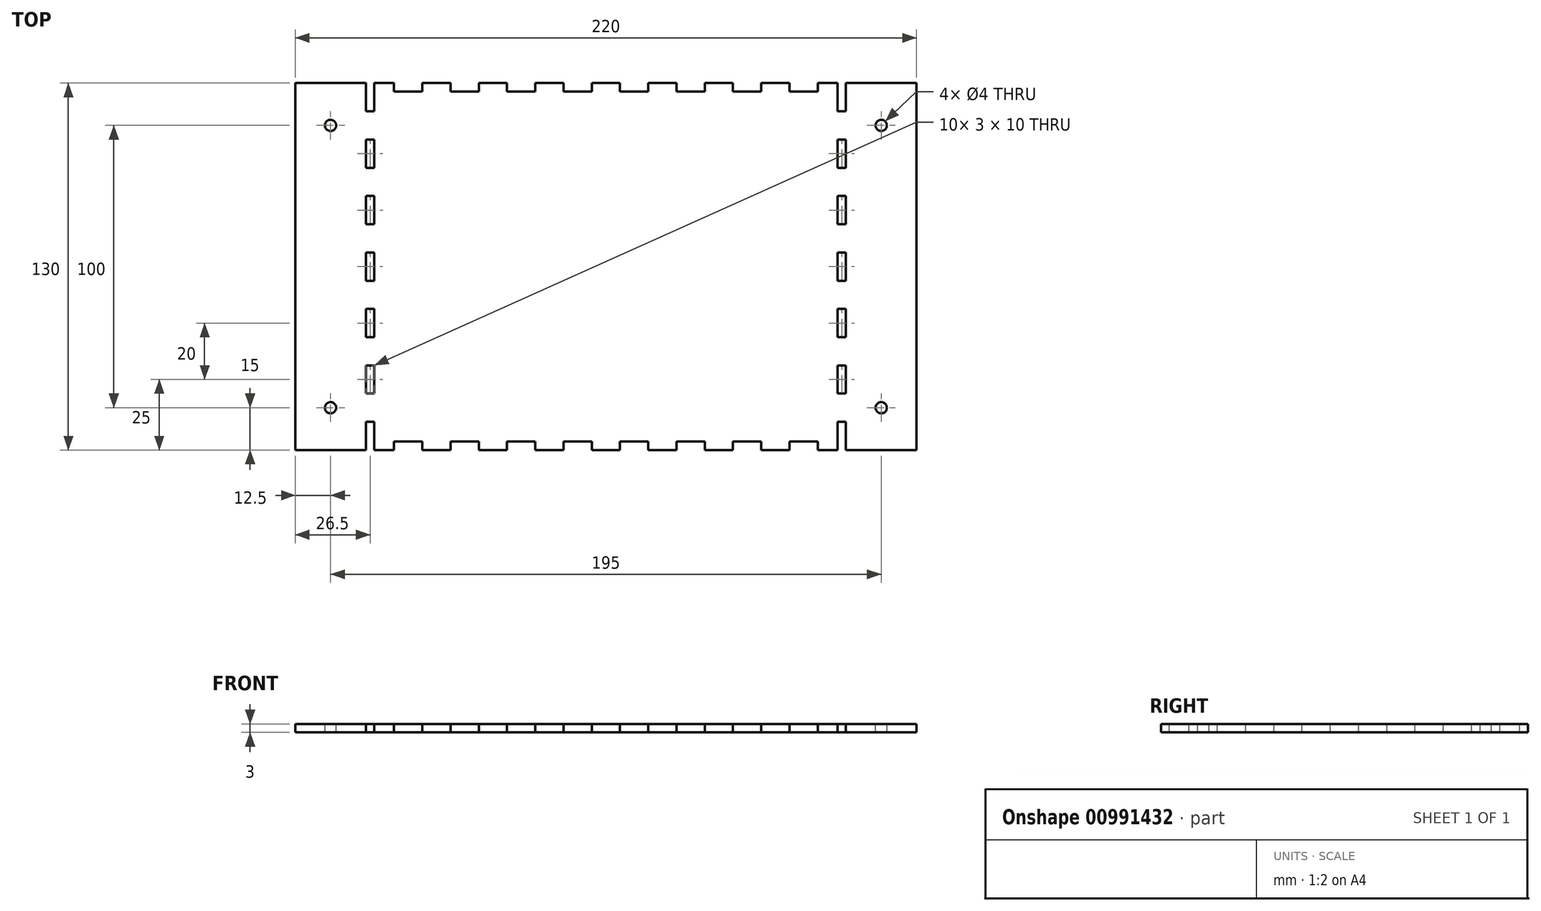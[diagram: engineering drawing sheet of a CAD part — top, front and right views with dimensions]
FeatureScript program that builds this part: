
annotation { "Feature Type Name" : "Feature", "Feature Type Description" : "" }
export const myFeature = defineFeature(function(context is Context, id is Id, definition is map)
    precondition{}
    {
        {
            var Q0;
            Q0=qCreatedBy(makeId("Top.planeOp"),FACE);
            var sketch = newSketch(context, id + "F0", { "sketchPlane" : qUnion([Q0])});
            skLineSegment(sketch, "E0.bottom", {"start": v(110, -65) * mm, "end": v(-110, -65) * mm});
            skLineSegment(sketch, "E0.top", {"start": v(110, 65) * mm, "end": v(-110, 65) * mm});
            skLineSegment(sketch, "E0.left", {"start": v(110, -65) * mm, "end": v(110, 65) * mm});
            skLineSegment(sketch, "E0.right", {"start": v(-110, -65) * mm, "end": v(-110, 65) * mm});
            skPoint(sketch, "E0.middle", {"position": v(0, 0) * mm});
            skSolve(sketch);
        }
        {
            var Q0;
            Q0 = qSketchRegion(id + "F0", true);
            extrude(context, id + "F1", {"entities" : qUnion([Q0]), "depth" : 3 * mm, "offsetDistance" : 25 * mm});
        }
        {
            var Q0;
            Q0=makeQuery(id+"F1.opExtrude","CAP_FACE",FACE,{"disambiguationData":[OSD([sQuery(id+"F0.wireOp",EDGE,"E0.bottom"),sQuery(id+"F0.wireOp",EDGE,"E0.top"),sQuery(id+"F0.wireOp",EDGE,"E0.left"),sQuery(id+"F0.wireOp",EDGE,"E0.right")])],"isStart":false});
            var sketch = newSketch(context, id + "F2", { "sketchPlane" : qUnion([Q0])});
            skLineSegment(sketch, "E1.bottom", {"start": v(-75, -65) * mm, "end": v(-65, -65) * mm});
            skLineSegment(sketch, "E1.top", {"start": v(-75, -62) * mm, "end": v(-65, -62) * mm});
            skLineSegment(sketch, "E1.right", {"start": v(-65, -65) * mm, "end": v(-65, -62) * mm});
            skLineSegment(sketch, "E2.1.0.0", {"start": v(-55, -65) * mm, "end": v(-45, -65) * mm});
            skLineSegment(sketch, "E2.1.0.1", {"start": v(-55, -62) * mm, "end": v(-45, -62) * mm});
            skLineSegment(sketch, "E2.1.0.2", {"start": v(-55, -65) * mm, "end": v(-55, -62) * mm});
            skLineSegment(sketch, "E2.1.0.3", {"start": v(-45, -65) * mm, "end": v(-45, -62) * mm});
            skLineSegment(sketch, "E2.2.0.0", {"start": v(-35, -65) * mm, "end": v(-25, -65) * mm});
            skLineSegment(sketch, "E2.2.0.1", {"start": v(-35, -62) * mm, "end": v(-25, -62) * mm});
            skLineSegment(sketch, "E2.2.0.2", {"start": v(-35, -65) * mm, "end": v(-35, -62) * mm});
            skLineSegment(sketch, "E2.2.0.3", {"start": v(-25, -65) * mm, "end": v(-25, -62) * mm});
            skLineSegment(sketch, "E2.3.0.0", {"start": v(-15, -65) * mm, "end": v(-5, -65) * mm});
            skLineSegment(sketch, "E2.3.0.1", {"start": v(-15, -62) * mm, "end": v(-5, -62) * mm});
            skLineSegment(sketch, "E2.3.0.2", {"start": v(-15, -65) * mm, "end": v(-15, -62) * mm});
            skLineSegment(sketch, "E2.3.0.3", {"start": v(-5, -65) * mm, "end": v(-5, -62) * mm});
            skLineSegment(sketch, "E2.4.0.0", {"start": v(5, -65) * mm, "end": v(15, -65) * mm});
            skLineSegment(sketch, "E2.4.0.1", {"start": v(5, -62) * mm, "end": v(15, -62) * mm});
            skLineSegment(sketch, "E2.4.0.2", {"start": v(5, -65) * mm, "end": v(5, -62) * mm});
            skLineSegment(sketch, "E2.4.0.3", {"start": v(15, -65) * mm, "end": v(15, -62) * mm});
            skLineSegment(sketch, "E2.5.0.0", {"start": v(25, -65) * mm, "end": v(35, -65) * mm});
            skLineSegment(sketch, "E2.5.0.1", {"start": v(25, -62) * mm, "end": v(35, -62) * mm});
            skLineSegment(sketch, "E2.5.0.2", {"start": v(25, -65) * mm, "end": v(25, -62) * mm});
            skLineSegment(sketch, "E2.5.0.3", {"start": v(35, -65) * mm, "end": v(35, -62) * mm});
            skLineSegment(sketch, "E2.6.0.0", {"start": v(45, -65) * mm, "end": v(55, -65) * mm});
            skLineSegment(sketch, "E2.6.0.1", {"start": v(45, -62) * mm, "end": v(55, -62) * mm});
            skLineSegment(sketch, "E2.6.0.2", {"start": v(45, -65) * mm, "end": v(45, -62) * mm});
            skLineSegment(sketch, "E2.6.0.3", {"start": v(55, -65) * mm, "end": v(55, -62) * mm});
            skLineSegment(sketch, "E2.7.0.0", {"start": v(65, -65) * mm, "end": v(75, -65) * mm});
            skLineSegment(sketch, "E2.7.0.1", {"start": v(65, -62) * mm, "end": v(75, -62) * mm});
            skLineSegment(sketch, "E2.7.0.2", {"start": v(65, -65) * mm, "end": v(65, -62) * mm});
            skLineSegment(sketch, "E2.7.0.3", {"start": v(75, -65) * mm, "end": v(75, -62) * mm});
            skLineSegment(sketch, "E2.direction1", {"start": v(-75, -65) * mm, "end": v(-55, -65) * mm, "construction": true});
            skLineSegment(sketch, "E3.direction1", {"start": v(-75, -65) * mm, "end": v(-50, -65) * mm, "construction": true});
            skLineSegment(sketch, "E4", {"start": v(-75, -62) * mm, "end": v(-75, -65) * mm});
            skLineSegment(sketch, "E5.bottom", {"start": v(-85, -65) * mm, "end": v(-82, -65) * mm});
            skLineSegment(sketch, "E5.top", {"start": v(-85, -55) * mm, "end": v(-82, -55) * mm});
            skLineSegment(sketch, "E5.left", {"start": v(-85, -65) * mm, "end": v(-85, -55) * mm});
            skLineSegment(sketch, "E5.right", {"start": v(-82, -65) * mm, "end": v(-82, -55) * mm});
            skLineSegment(sketch, "E6.0.1.0", {"start": v(-85, -45) * mm, "end": v(-85, -35) * mm});
            skLineSegment(sketch, "E6.0.1.1", {"start": v(-82, -45) * mm, "end": v(-82, -35) * mm});
            skLineSegment(sketch, "E6.0.1.2", {"start": v(-85, -35) * mm, "end": v(-82, -35) * mm});
            skLineSegment(sketch, "E6.0.1.3", {"start": v(-85, -45) * mm, "end": v(-82, -45) * mm});
            skLineSegment(sketch, "E6.0.2.0", {"start": v(-85, -25) * mm, "end": v(-85, -15) * mm});
            skLineSegment(sketch, "E6.0.2.1", {"start": v(-82, -25) * mm, "end": v(-82, -15) * mm});
            skLineSegment(sketch, "E6.0.2.2", {"start": v(-85, -15) * mm, "end": v(-82, -15) * mm});
            skLineSegment(sketch, "E6.0.2.3", {"start": v(-85, -25) * mm, "end": v(-82, -25) * mm});
            skLineSegment(sketch, "E6.0.3.0", {"start": v(-85, -5) * mm, "end": v(-85, 5) * mm});
            skLineSegment(sketch, "E6.0.3.1", {"start": v(-82, -5) * mm, "end": v(-82, 5) * mm});
            skLineSegment(sketch, "E6.0.3.2", {"start": v(-85, 5) * mm, "end": v(-82, 5) * mm});
            skLineSegment(sketch, "E6.0.3.3", {"start": v(-85, -5) * mm, "end": v(-82, -5) * mm});
            skLineSegment(sketch, "E6.0.4.0", {"start": v(-85, 15) * mm, "end": v(-85, 25) * mm});
            skLineSegment(sketch, "E6.0.4.1", {"start": v(-82, 15) * mm, "end": v(-82, 25) * mm});
            skLineSegment(sketch, "E6.0.4.2", {"start": v(-85, 25) * mm, "end": v(-82, 25) * mm});
            skLineSegment(sketch, "E6.0.4.3", {"start": v(-85, 15) * mm, "end": v(-82, 15) * mm});
            skLineSegment(sketch, "E6.0.5.0", {"start": v(-85, 35) * mm, "end": v(-85, 45) * mm});
            skLineSegment(sketch, "E6.0.5.1", {"start": v(-82, 35) * mm, "end": v(-82, 45) * mm});
            skLineSegment(sketch, "E6.0.5.2", {"start": v(-85, 45) * mm, "end": v(-82, 45) * mm});
            skLineSegment(sketch, "E6.0.5.3", {"start": v(-85, 35) * mm, "end": v(-82, 35) * mm});
            skLineSegment(sketch, "E6.0.6.0", {"start": v(-85, 55) * mm, "end": v(-85, 65) * mm});
            skLineSegment(sketch, "E6.0.6.1", {"start": v(-82, 55) * mm, "end": v(-82, 65) * mm});
            skLineSegment(sketch, "E6.0.6.2", {"start": v(-85, 65) * mm, "end": v(-82, 65) * mm});
            skLineSegment(sketch, "E6.0.6.3", {"start": v(-85, 55) * mm, "end": v(-82, 55) * mm});
            skLineSegment(sketch, "E6.direction1", {"start": v(-85, -65) * mm, "end": v(-60, -65) * mm, "construction": true});
            skLineSegment(sketch, "E6.direction2", {"start": v(-85, -65) * mm, "end": v(-85, -45) * mm, "construction": true});
            skLineSegment(sketch, "E7", {"start": v(-110, 0) * mm, "end": v(110, 0) * mm, "construction": true});
            skLineSegment(sketch, "E8.MirrorCS", {"start": v(-45, 65) * mm, "end": v(-45, 62) * mm});
            skLineSegment(sketch, "E9.MirrorCS", {"start": v(25, 65) * mm, "end": v(25, 62) * mm});
            skLineSegment(sketch, "E10.MirrorCS", {"start": v(-75, 62) * mm, "end": v(-75, 65) * mm});
            skLineSegment(sketch, "E11.MirrorCS", {"start": v(65, 65) * mm, "end": v(65, 62) * mm});
            skLineSegment(sketch, "E12.MirrorCS", {"start": v(-15, 65) * mm, "end": v(-15, 62) * mm});
            skLineSegment(sketch, "E13.MirrorCS", {"start": v(-75, 65) * mm, "end": v(-65, 65) * mm});
            skLineSegment(sketch, "E14.MirrorCS", {"start": v(-25, 65) * mm, "end": v(-25, 62) * mm});
            skLineSegment(sketch, "E15.MirrorCS", {"start": v(-55, 65) * mm, "end": v(-55, 62) * mm});
            skLineSegment(sketch, "E16.MirrorCS", {"start": v(-65, 65) * mm, "end": v(-65, 62) * mm});
            skLineSegment(sketch, "E17.MirrorCS", {"start": v(75, 65) * mm, "end": v(75, 62) * mm});
            skLineSegment(sketch, "E18.MirrorCS", {"start": v(-5, 65) * mm, "end": v(-5, 62) * mm});
            skLineSegment(sketch, "E19.MirrorCS", {"start": v(55, 65) * mm, "end": v(55, 62) * mm});
            skLineSegment(sketch, "E20.MirrorCS", {"start": v(45, 65) * mm, "end": v(45, 62) * mm});
            skLineSegment(sketch, "E21.MirrorCS", {"start": v(5, 65) * mm, "end": v(5, 62) * mm});
            skLineSegment(sketch, "E22.MirrorCS", {"start": v(15, 65) * mm, "end": v(15, 62) * mm});
            skLineSegment(sketch, "E23.MirrorCS", {"start": v(-35, 65) * mm, "end": v(-35, 62) * mm});
            skLineSegment(sketch, "E24.MirrorCS", {"start": v(35, 65) * mm, "end": v(35, 62) * mm});
            skLineSegment(sketch, "E25.MirrorCS", {"start": v(-75, 65) * mm, "end": v(-55, 65) * mm, "construction": true});
            skLineSegment(sketch, "E26.MirrorCS", {"start": v(-55, 65) * mm, "end": v(-45, 65) * mm});
            skLineSegment(sketch, "E27.MirrorCS", {"start": v(25, 62) * mm, "end": v(35, 62) * mm});
            skLineSegment(sketch, "E28.MirrorCS", {"start": v(-35, 62) * mm, "end": v(-25, 62) * mm});
            skLineSegment(sketch, "E29.MirrorCS", {"start": v(-35, 65) * mm, "end": v(-25, 65) * mm});
            skLineSegment(sketch, "E30.MirrorCS", {"start": v(25, 65) * mm, "end": v(35, 65) * mm});
            skLineSegment(sketch, "E31.MirrorCS", {"start": v(-15, 62) * mm, "end": v(-5, 62) * mm});
            skLineSegment(sketch, "E32.MirrorCS", {"start": v(-75, 62) * mm, "end": v(-65, 62) * mm});
            skLineSegment(sketch, "E33.MirrorCS", {"start": v(-15, 65) * mm, "end": v(-5, 65) * mm});
            skLineSegment(sketch, "E34.MirrorCS", {"start": v(45, 65) * mm, "end": v(55, 65) * mm});
            skLineSegment(sketch, "E35.MirrorCS", {"start": v(-75, 65) * mm, "end": v(-50, 65) * mm, "construction": true});
            skLineSegment(sketch, "E36.MirrorCS", {"start": v(45, 62) * mm, "end": v(55, 62) * mm});
            skLineSegment(sketch, "E37.MirrorCS", {"start": v(-55, 62) * mm, "end": v(-45, 62) * mm});
            skLineSegment(sketch, "E38.MirrorCS", {"start": v(5, 65) * mm, "end": v(15, 65) * mm});
            skLineSegment(sketch, "E39.MirrorCS", {"start": v(65, 65) * mm, "end": v(75, 65) * mm});
            skLineSegment(sketch, "E40.MirrorCS", {"start": v(5, 62) * mm, "end": v(15, 62) * mm});
            skLineSegment(sketch, "E41.MirrorCS", {"start": v(65, 62) * mm, "end": v(75, 62) * mm});
            skLineSegment(sketch, "E42", {"start": v(0, 65) * mm, "end": v(0, -62) * mm, "construction": true});
            skLineSegment(sketch, "E43.MirrorCS", {"start": v(85, -45) * mm, "end": v(82, -45) * mm});
            skLineSegment(sketch, "E44.MirrorCS", {"start": v(85, -25) * mm, "end": v(82, -25) * mm});
            skLineSegment(sketch, "E45.MirrorCS", {"start": v(85, 35) * mm, "end": v(82, 35) * mm});
            skLineSegment(sketch, "E46.MirrorCS", {"start": v(85, 55) * mm, "end": v(82, 55) * mm});
            skLineSegment(sketch, "E47.MirrorCS", {"start": v(85, 45) * mm, "end": v(82, 45) * mm});
            skLineSegment(sketch, "E48.MirrorCS", {"start": v(85, 15) * mm, "end": v(82, 15) * mm});
            skLineSegment(sketch, "E49.MirrorCS", {"start": v(85, 65) * mm, "end": v(82, 65) * mm});
            skLineSegment(sketch, "E50.MirrorCS", {"start": v(85, -65) * mm, "end": v(82, -65) * mm});
            skLineSegment(sketch, "E51.MirrorCS", {"start": v(85, -5) * mm, "end": v(82, -5) * mm});
            skLineSegment(sketch, "E52.MirrorCS", {"start": v(85, -15) * mm, "end": v(82, -15) * mm});
            skLineSegment(sketch, "E53.MirrorCS", {"start": v(85, -55) * mm, "end": v(82, -55) * mm});
            skLineSegment(sketch, "E54.MirrorCS", {"start": v(85, 25) * mm, "end": v(82, 25) * mm});
            skLineSegment(sketch, "E55.MirrorCS", {"start": v(85, 5) * mm, "end": v(82, 5) * mm});
            skLineSegment(sketch, "E56.MirrorCS", {"start": v(85, -35) * mm, "end": v(82, -35) * mm});
            skLineSegment(sketch, "E57.MirrorCS", {"start": v(85, -65) * mm, "end": v(85, -55) * mm});
            skLineSegment(sketch, "E58.MirrorCS", {"start": v(85, 15) * mm, "end": v(85, 25) * mm});
            skLineSegment(sketch, "E59.MirrorCS", {"start": v(82, -45) * mm, "end": v(82, -35) * mm});
            skLineSegment(sketch, "E60.MirrorCS", {"start": v(82, -25) * mm, "end": v(82, -15) * mm});
            skLineSegment(sketch, "E61.MirrorCS", {"start": v(85, -5) * mm, "end": v(85, 5) * mm});
            skLineSegment(sketch, "E62.MirrorCS", {"start": v(82, -5) * mm, "end": v(82, 5) * mm});
            skLineSegment(sketch, "E63.MirrorCS", {"start": v(85, -65) * mm, "end": v(85, -45) * mm, "construction": true});
            skLineSegment(sketch, "E64.MirrorCS", {"start": v(85, -45) * mm, "end": v(85, -35) * mm});
            skLineSegment(sketch, "E65.MirrorCS", {"start": v(82, 15) * mm, "end": v(82, 25) * mm});
            skLineSegment(sketch, "E66.MirrorCS", {"start": v(82, -65) * mm, "end": v(82, -55) * mm});
            skLineSegment(sketch, "E67.MirrorCS", {"start": v(85, -25) * mm, "end": v(85, -15) * mm});
            skLineSegment(sketch, "E68.MirrorCS", {"start": v(82, 35) * mm, "end": v(82, 45) * mm});
            skLineSegment(sketch, "E69.MirrorCS", {"start": v(82, 55) * mm, "end": v(82, 65) * mm});
            skLineSegment(sketch, "E70.MirrorCS", {"start": v(85, 35) * mm, "end": v(85, 45) * mm});
            skLineSegment(sketch, "E71.MirrorCS", {"start": v(85, 55) * mm, "end": v(85, 65) * mm});
            skSolve(sketch);
        }
        {
            var Q0;
            Q0 = qSketchRegion(id + "F2", true);
            extrude(context, id + "F3", {"entities" : qUnion([Q0]), "operationType" : NewBodyOperationType.REMOVE, "endBound" : BoundingType.THROUGH_ALL, "oppositeDirection" : true, "depth" : 25 * mm, "offsetDistance" : 25 * mm});
        }
        {
            var Q0;
            Q0=makeQuery(id+"F1.opExtrude","CAP_FACE",FACE,{"disambiguationData":[OSD([sQuery(id+"F0.wireOp",EDGE,"E0.bottom"),sQuery(id+"F0.wireOp",EDGE,"E0.top"),sQuery(id+"F0.wireOp",EDGE,"E0.left"),sQuery(id+"F0.wireOp",EDGE,"E0.right")])],"isStart":false});
            var sketch = newSketch(context, id + "F4", { "sketchPlane" : qUnion([Q0])});
            skLineSegment(sketch, "E72", {"start": v(97.5, 65) * mm, "end": v(97.5, -65) * mm, "construction": true});
            skCircle(sketch, "E73", {"center": v(97.5, 50) * mm, "radius": 2 * mm});
            skLineSegment(sketch, "E74", {"start": v(-110, 0) * mm, "end": v(110, 0) * mm, "construction": true});
            skCircle(sketch, "E75.MirrorC", {"center": v(97.5, -50) * mm, "radius": 2 * mm});
            skLineSegment(sketch, "E76", {"start": v(0, 65) * mm, "end": v(0, -65) * mm, "construction": true});
            skCircle(sketch, "E77.MirrorC", {"center": v(-97.5, 50) * mm, "radius": 2 * mm});
            skCircle(sketch, "E78.MirrorC", {"center": v(-97.5, -50) * mm, "radius": 2 * mm});
            skSolve(sketch);
        }
        {
            var Q0;
            Q0 = qSketchRegion(id + "F4", true);
            extrude(context, id + "F5", {"entities" : qUnion([Q0]), "operationType" : NewBodyOperationType.REMOVE, "endBound" : BoundingType.THROUGH_ALL, "oppositeDirection" : true, "depth" : 25 * mm, "offsetDistance" : 25 * mm});
        }
    });
